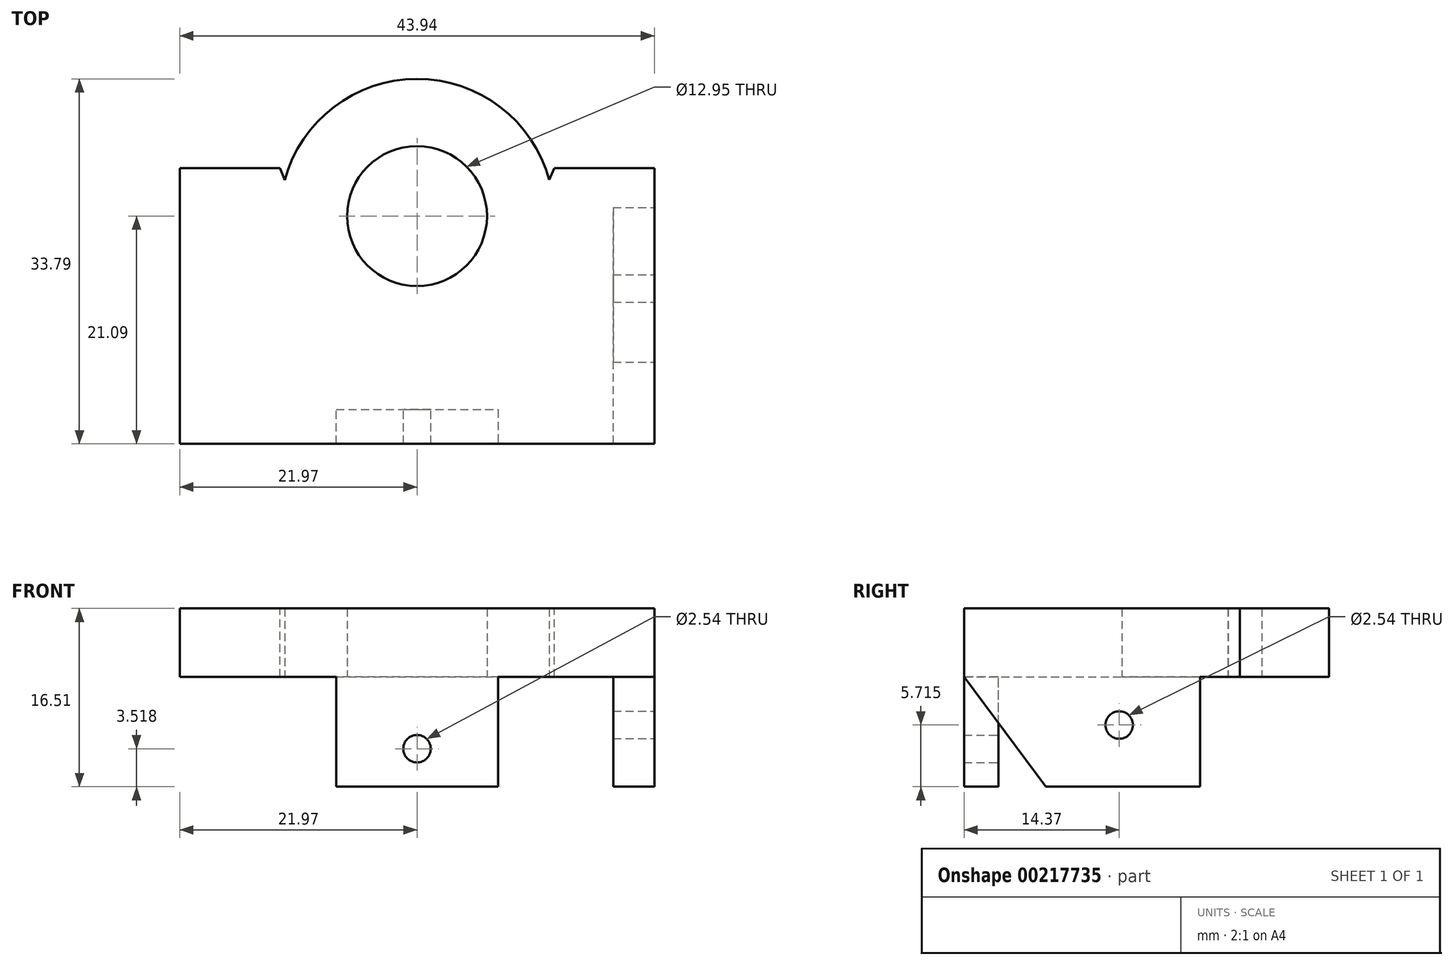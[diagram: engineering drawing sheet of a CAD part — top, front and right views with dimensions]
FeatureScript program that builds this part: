
annotation { "Feature Type Name" : "Feature", "Feature Type Description" : "" }
export const myFeature = defineFeature(function(context is Context, id is Id, definition is map)
    precondition{}
    {
        {
            var Q0;
            Q0=qCreatedBy(makeId("Top.planeOp"),FACE);
            var sketch = newSketch(context, id + "F0", { "sketchPlane" : qUnion([Q0])});
            skCircle(sketch, "E0", {"center": v(0, 0) * mm, "radius": 6.48 * mm});
            skCircle(sketch, "E1", {"center": v(0, 0) * mm, "radius": 12.7 * mm});
            skSolve(sketch);
        }
        {
            var Q0;
            Q0=qSketchRegion(id+"F0",true);
            extrude(context, id + "F1", {"entities" : qUnion([Q0]), "depth" : 6.35 * mm});
        }
        {
            var Q0;
            Q0=makeQuery(id+"F1.opExtrude","CAP_FACE",FACE,{"disambiguationData":[OSD([sQuery(id+"F0.wireOp",EDGE,"E0"),sQuery(id+"F0.wireOp",EDGE,"E1")])],"isStart":false});
            var sketch = newSketch(context, id + "F2", { "sketchPlane" : qUnion([Q0])});
            skLineSegment(sketch, "E2", {"start": v(0, -21.09) * mm, "end": v(-21.97, -21.09) * mm});
            skLineSegment(sketch, "E3", {"start": v(0, -21.09) * mm, "end": v(21.97, -21.09) * mm});
            skLineSegment(sketch, "E4", {"start": v(21.97, -21.09) * mm, "end": v(21.97, -17.91) * mm});
            skLineSegment(sketch, "E5", {"start": v(-21.97, -21.09) * mm, "end": v(-21.97, -17.9) * mm});
            skLineSegment(sketch, "E6", {"start": v(21.97, -17.91) * mm, "end": v(21.97, 4.45) * mm});
            skLineSegment(sketch, "E7", {"start": v(21.97, 4.45) * mm, "end": v(12.7, 4.45) * mm});
            skLineSegment(sketch, "E8", {"start": v(-21.97, -17.9) * mm, "end": v(-21.97, 4.45) * mm});
            skLineSegment(sketch, "E9", {"start": v(-21.97, 4.45) * mm, "end": v(-12.7, 4.45) * mm});
            skLineSegment(sketch, "E10", {"start": v(-12.7, 4.45) * mm, "end": v(-6.95, -9.77) * mm});
            skLineSegment(sketch, "E11", {"start": v(-6.95, -9.77) * mm, "end": v(6.77, -9.77) * mm});
            skLineSegment(sketch, "E12", {"start": v(6.77, -9.77) * mm, "end": v(12.7, 4.45) * mm});
            skSolve(sketch);
        }
        {
            var Q0;
            Q0=qSketchRegion(id+"F2",true);
            extrude(context, id + "F3", {"entities" : qUnion([Q0]), "operationType" : NewBodyOperationType.ADD, "oppositeDirection" : true, "depth" : 6.35 * mm});
        }
        {
            var Q0;
            Q0=makeQuery(id+"F3.opExtrude","SWEPT_FACE",FACE,{"disambiguationData":[OSD([sQuery(id+"F2.wireOp",EDGE,"E4")])]});
            var sketch = newSketch(context, id + "F4", { "sketchPlane" : qUnion([Q0])});
            skLineSegment(sketch, "E13", {"start": v(-21.09, 6.35) * mm, "end": v(0.78, 6.35) * mm});
            skLineSegment(sketch, "E14", {"start": v(0.78, 6.35) * mm, "end": v(0.78, -10.16) * mm});
            skLineSegment(sketch, "E15", {"start": v(0.78, -10.16) * mm, "end": v(-13.53, -10.16) * mm});
            skLineSegment(sketch, "E16", {"start": v(-21.09, 0) * mm, "end": v(-21.09, 6.35) * mm});
            skLineSegment(sketch, "E17", {"start": v(0.78, -10.16) * mm, "end": v(-6.72, -10.16) * mm});
            skLineSegment(sketch, "E18", {"start": v(-6.72, -10.16) * mm, "end": v(-6.72, -4.45) * mm});
            skPoint(sketch, "E18.endSnap0", {"position": v(0.78, -1.9) * mm});
            skCircle(sketch, "E19", {"center": v(-6.72, -4.45) * mm, "radius": 1.27 * mm});
            skLineSegment(sketch, "E20", {"start": v(-21.09, 0) * mm, "end": v(-13.53, -10.16) * mm});
            skPoint(sketch, "E21.orphan", {"position": v(-21.09, -10.16) * mm});
            skPoint(sketch, "E22.orphan", {"position": v(-6.72, -1.9) * mm});
            skSolve(sketch);
        }
        {
            var Q0;
            Q0=qSketchRegion(id+"F4",true);
            extrude(context, id + "F5", {"entities" : qUnion([Q0]), "operationType" : NewBodyOperationType.ADD, "oppositeDirection" : true, "depth" : 3.8 * mm});
        }
        {
            var Q0;
            Q0=makeQuery(id+"F3.boolean.opBoolean","MERGE",FACE,{"derivedFrom":[makeQuery(id+"F1.opExtrude","CAP_FACE",FACE,{"disambiguationData":[OSD([sQuery(id+"F0.wireOp",EDGE,"E0"),sQuery(id+"F0.wireOp",EDGE,"E1")])],"isStart":true}),makeQuery(id+"F3.opExtrude","CAP_FACE",FACE,{"disambiguationData":[OSD([sQuery(id+"F2.wireOp",EDGE,"E2"),sQuery(id+"F2.wireOp",EDGE,"E3"),sQuery(id+"F2.wireOp",EDGE,"E4"),sQuery(id+"F2.wireOp",EDGE,"E5"),sQuery(id+"F2.wireOp",EDGE,"ihHadCWb-XjeW-R3a0-dGNE-DLv68DcTVQ7N"),sQuery(id+"F2.wireOp",EDGE,"1IoPUFMC-zjit-IGW3-BYE7-LK0CDHMM8rKh"),sQuery(id+"F2.wireOp",EDGE,"NdcEkIWE-Nxbb-I5WJ-c0X4-1hDUIVkZ8ckX"),sQuery(id+"F2.wireOp",EDGE,"YiZrzofx-tHcN-ggQp-RaR3-rrEU8t4WHX24"),sQuery(id+"F2.wireOp",EDGE,"RK1YeRvc-nPOg-Eqkx-etu6-UXfsHSOCRuCc"),sQuery(id+"F2.wireOp",EDGE,"3zleHhUL-0sEu-ddFR-184l-ClsJvtk2H4PM")])],"isStart":false})]});
            var sketch = newSketch(context, id + "F6", { "sketchPlane" : qUnion([Q0])});
            skLineSegment(sketch, "E23", {"start": v(0, 21.09) * mm, "end": v(7.5, 21.09) * mm});
            skLineSegment(sketch, "E24", {"start": v(0, 21.09) * mm, "end": v(-7.5, 21.09) * mm});
            skLineSegment(sketch, "E25", {"start": v(-7.5, 21.09) * mm, "end": v(-7.5, 17.91) * mm});
            skLineSegment(sketch, "E26", {"start": v(-7.5, 17.91) * mm, "end": v(7.5, 17.91) * mm});
            skLineSegment(sketch, "E27", {"start": v(7.5, 17.91) * mm, "end": v(7.5, 21.09) * mm});
            skSolve(sketch);
        }
        {
            var Q0;
            Q0=qSketchRegion(id+"F6",true);
            extrude(context, id + "F7", {"entities" : qUnion([Q0]), "operationType" : NewBodyOperationType.ADD, "depth" : 10.16 * mm});
        }
        {
            var Q0;
            Q0=makeQuery(id+"F7.opExtrude","SWEPT_FACE",FACE,{"disambiguationData":[OSD([sQuery(id+"F6.wireOp",EDGE,"E26")])]});
            var sketch = newSketch(context, id + "F8", { "sketchPlane" : qUnion([Q0])});
            skLineSegment(sketch, "E28", {"start": v(0, -10.16) * mm, "end": v(0, -6.64) * mm});
            skPoint(sketch, "E28.endSnap0", {"position": v(0, -10.16) * mm});
            skCircle(sketch, "E29", {"center": v(0, -6.64) * mm, "radius": 1.27 * mm});
            skSolve(sketch);
        }
        {
            var Q0;
            Q0=qSketchRegion(id+"F8",true);
            extrude(context, id + "F9", {"entities" : qUnion([Q0]), "operationType" : NewBodyOperationType.REMOVE, "oppositeDirection" : true, "depth" : 25.4 * mm});
        }
    });
